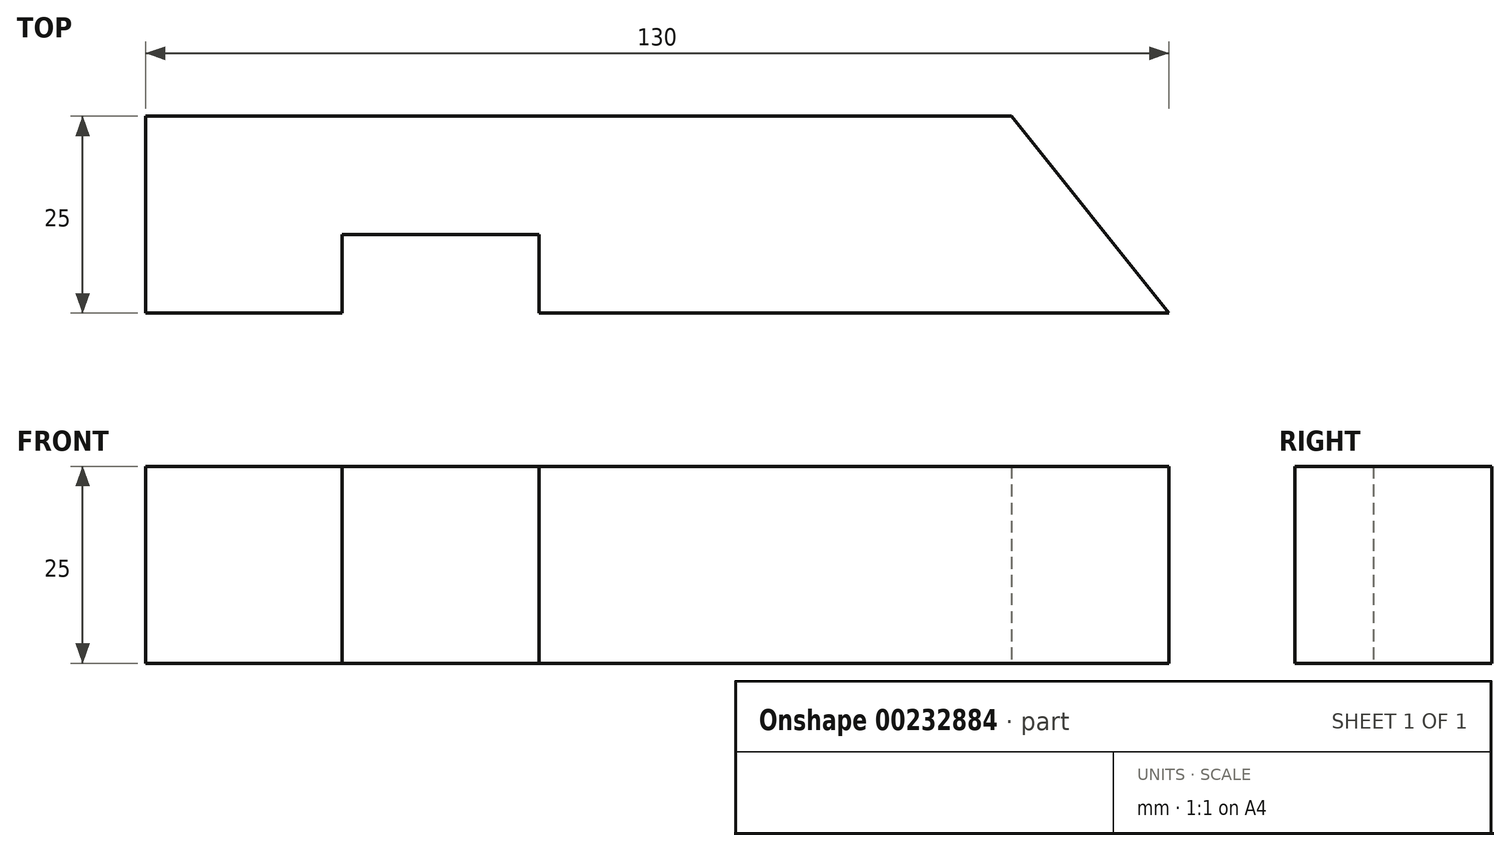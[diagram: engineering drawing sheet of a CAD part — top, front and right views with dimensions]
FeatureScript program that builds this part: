
annotation { "Feature Type Name" : "Feature", "Feature Type Description" : "" }
export const myFeature = defineFeature(function(context is Context, id is Id, definition is map)
    precondition{}
    {
        {
            var Q0;
            Q0=qCreatedBy(makeId("Top.planeOp"),FACE);
            var sketch = newSketch(context, id + "F0", { "sketchPlane" : qUnion([Q0])});
            skLineSegment(sketch, "E0", {"start": v(-64.1, 43.1) * mm, "end": v(45.9, 43.1) * mm});
            skLineSegment(sketch, "E1", {"start": v(45.9, 43.1) * mm, "end": v(65.9, 18.1) * mm});
            skLineSegment(sketch, "E2", {"start": v(65.9, 18.1) * mm, "end": v(-14.1, 18.1) * mm});
            skLineSegment(sketch, "E3", {"start": v(-14.1, 18.1) * mm, "end": v(-14.1, 28.1) * mm});
            skLineSegment(sketch, "E4", {"start": v(-39.1, 28.1) * mm, "end": v(-39.1, 18.1) * mm});
            skLineSegment(sketch, "E5", {"start": v(-39.1, 18.1) * mm, "end": v(-64.1, 18.1) * mm});
            skLineSegment(sketch, "E6", {"start": v(-64.1, 43.1) * mm, "end": v(-64.1, 18.1) * mm});
            skLineSegment(sketch, "E7", {"start": v(-39.1, 28.1) * mm, "end": v(-14.1, 28.1) * mm});
            skSolve(sketch);
        }
        {
            var Q0;
            Q0 = qSketchRegion(id + "F0", true);
            extrude(context, id + "F1", {"entities" : qUnion([Q0]), "depth" : 25 * mm});
        }
    });
